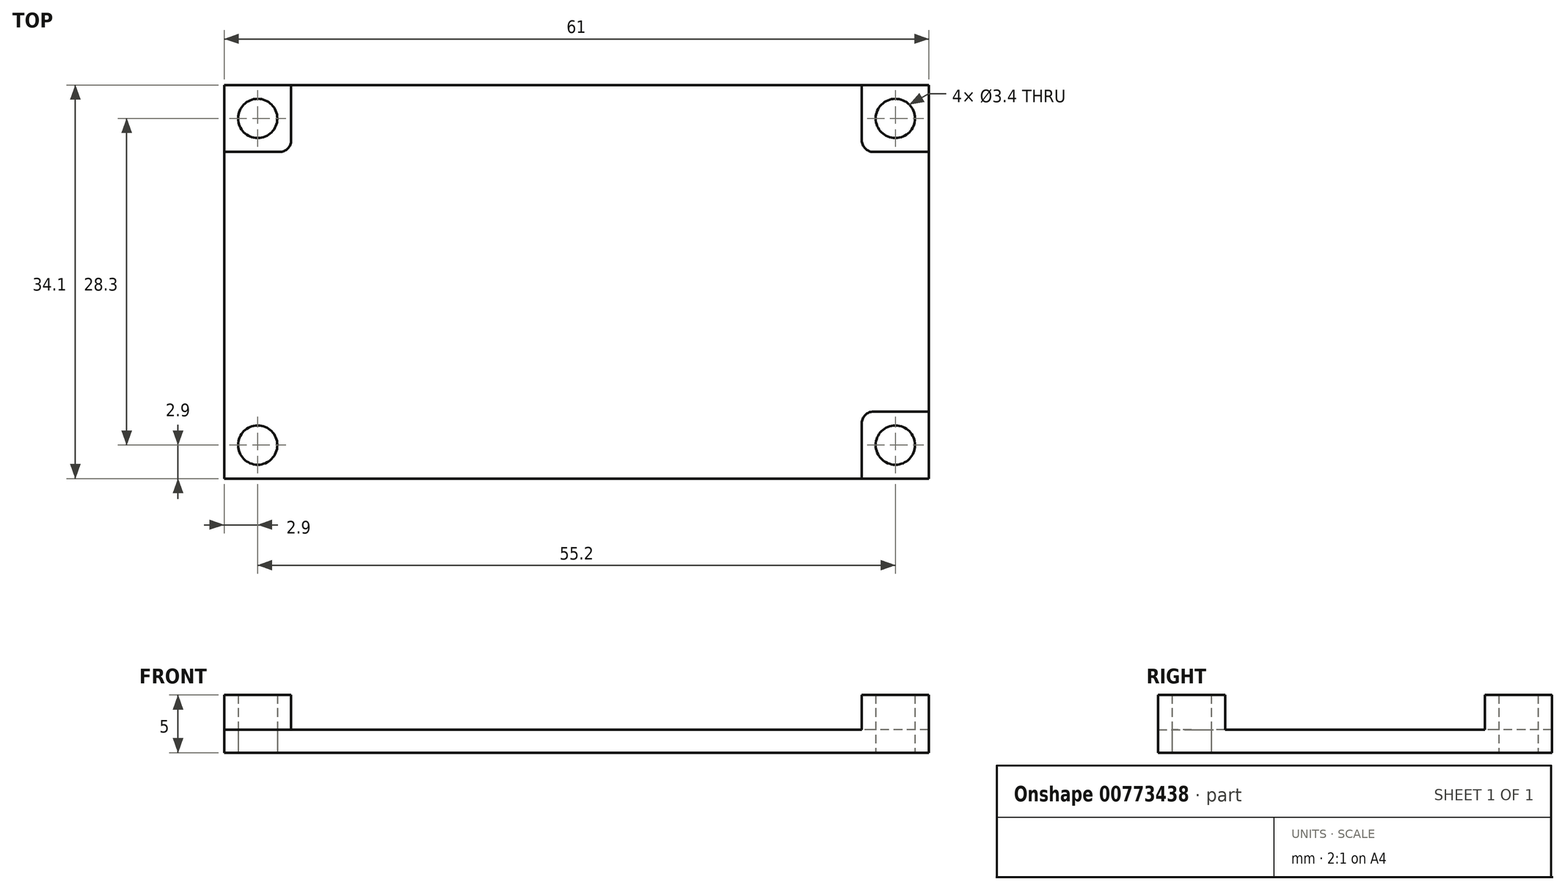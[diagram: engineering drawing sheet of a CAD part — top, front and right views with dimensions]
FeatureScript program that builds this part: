
annotation { "Feature Type Name" : "Feature", "Feature Type Description" : "" }
export const myFeature = defineFeature(function(context is Context, id is Id, definition is map)
    precondition{}
    {
        {
            var Q0;
            Q0=qCreatedBy(makeId("Top.planeOp"),FACE);
            var sketch = newSketch(context, id + "F0", { "sketchPlane" : qUnion([Q0])});
            skLineSegment(sketch, "E0.bottom", {"start": v(30.5, 17.05) * mm, "end": v(-30.5, 17.05) * mm});
            skLineSegment(sketch, "E0.top", {"start": v(30.5, -17.05) * mm, "end": v(-30.5, -17.05) * mm});
            skLineSegment(sketch, "E0.left", {"start": v(30.5, 17.05) * mm, "end": v(30.5, -17.05) * mm});
            skLineSegment(sketch, "E0.right", {"start": v(-30.5, 17.05) * mm, "end": v(-30.5, -17.05) * mm});
            skPoint(sketch, "E0.middle", {"position": v(0, 0) * mm});
            skLineSegment(sketch, "E1.bottom", {"start": v(-27.6, 17.05) * mm, "end": v(27.6, 17.05) * mm, "construction": true});
            skLineSegment(sketch, "E1.top", {"start": v(-27.6, 17.05) * mm, "end": v(27.6, 17.05) * mm, "construction": true});
            skLineSegment(sketch, "E1.left", {"start": v(-27.6, 17.05) * mm, "end": v(-27.6, 17.05) * mm});
            skLineSegment(sketch, "E1.right", {"start": v(27.6, 17.05) * mm, "end": v(27.6, 17.05) * mm});
            skPoint(sketch, "E1.middle", {"position": v(0, 17.05) * mm});
            skLineSegment(sketch, "E2.bottom", {"start": v(-30.5, 14.15) * mm, "end": v(-30.5, 14.15) * mm});
            skLineSegment(sketch, "E2.top", {"start": v(-30.5, -14.15) * mm, "end": v(-30.5, -14.15) * mm});
            skLineSegment(sketch, "E2.left", {"start": v(-30.5, 14.15) * mm, "end": v(-30.5, -14.15) * mm, "construction": true});
            skLineSegment(sketch, "E2.right", {"start": v(-30.5, 14.15) * mm, "end": v(-30.5, -14.15) * mm, "construction": true});
            skPoint(sketch, "E2.middle", {"position": v(-30.5, 0) * mm});
            skPoint(sketch, "E3", {"position": v(-27.6, 14.15) * mm});
            skPoint(sketch, "E4", {"position": v(-27.6, -14.15) * mm});
            skPoint(sketch, "E5", {"position": v(27.6, -14.15) * mm});
            skPoint(sketch, "E6", {"position": v(27.6, 14.15) * mm});
            skSolve(sketch);
        }
        {
            var Q0;
            Q0 = qSketchRegion(id + "F0", true);
            extrude(context, id + "F1", {"entities" : qUnion([Q0]), "depth" : 2 * mm, "offsetDistance" : 25 * mm});
        }
        {
            var Q0;
            Q0=makeQuery(id+"F1.opExtrude","CAP_FACE",FACE,{"disambiguationData":[OSD([sQuery(id+"F0.wireOp",EDGE,"E0.bottom"),sQuery(id+"F0.wireOp",EDGE,"E0.top"),sQuery(id+"F0.wireOp",EDGE,"E0.left"),sQuery(id+"F0.wireOp",EDGE,"E0.right")])],"isStart":false});
            var sketch = newSketch(context, id + "F2", { "sketchPlane" : qUnion([Q0])});
            skLineSegment(sketch, "E7", {"start": v(-27.6, 14.15) * mm, "end": v(-30.5, 14.15) * mm, "construction": true});
            skLineSegment(sketch, "E8", {"start": v(-27.6, 14.15) * mm, "end": v(-24.7, 14.15) * mm, "construction": true});
            skLineSegment(sketch, "E9.bottom", {"start": v(-30.5, 17.05) * mm, "end": v(-24.7, 17.05) * mm});
            skLineSegment(sketch, "E9.top", {"start": v(-30.5, 11.25) * mm, "end": v(-25.7, 11.25) * mm});
            skLineSegment(sketch, "E9.left", {"start": v(-30.5, 17.05) * mm, "end": v(-30.5, 11.25) * mm});
            skLineSegment(sketch, "E9.right", {"start": v(-24.7, 17.05) * mm, "end": v(-24.7, 12.25) * mm});
            skPoint(sketch, "E10.visualSharp", {"position": v(-24.7, 11.25) * mm});
            skArc(sketch, "E10.filletArc", {"start": v(-25.7, 11.25) * mm, "mid": v(-25, 11.54) * mm, "end": v(-24.7, 12.25) * mm});
            skLineSegment(sketch, "E11", {"start": v(-24.7, 11.25) * mm, "end": v(-30.5, 11.25) * mm, "construction": true});
            skLineSegment(sketch, "E12", {"start": v(-24.7, 11.25) * mm, "end": v(-24.7, -17.05) * mm, "construction": true});
            skLineSegment(sketch, "E13", {"start": v(-24.7, 11.25) * mm, "end": v(30.5, 11.25) * mm, "construction": true});
            skLineSegment(sketch, "E14", {"start": v(-24.7, -17.05) * mm, "end": v(-24.7, -12.25) * mm});
            skLineSegment(sketch, "E15", {"start": v(-24.7, -11.25) * mm, "end": v(30.5, -11.25) * mm, "construction": true});
            skLineSegment(sketch, "E16", {"start": v(30.5, -11.25) * mm, "end": v(24.7, -11.25) * mm, "construction": true});
            skLineSegment(sketch, "E17", {"start": v(24.7, -17.05) * mm, "end": v(24.7, 17.05) * mm, "construction": true});
            skLineSegment(sketch, "E18", {"start": v(24.7, 17.05) * mm, "end": v(24.7, 12.25) * mm});
            skLineSegment(sketch, "E19", {"start": v(25.7, 11.25) * mm, "end": v(30.5, 11.25) * mm});
            skLineSegment(sketch, "E20", {"start": v(30.5, -11.25) * mm, "end": v(25.7, -11.25) * mm});
            skLineSegment(sketch, "E21", {"start": v(24.7, -17.05) * mm, "end": v(24.7, -12.25) * mm});
            skPoint(sketch, "E22.visualSharp", {"position": v(-24.7, -11.25) * mm});
            skPoint(sketch, "E23.visualSharp", {"position": v(24.7, -11.25) * mm});
            skArc(sketch, "E23.filletArc", {"start": v(25.7, -11.25) * mm, "mid": v(25, -11.54) * mm, "end": v(24.7, -12.25) * mm});
            skPoint(sketch, "E24.visualSharp", {"position": v(24.7, 11.25) * mm});
            skArc(sketch, "E24.filletArc", {"start": v(24.7, 12.25) * mm, "mid": v(25, 11.54) * mm, "end": v(25.7, 11.25) * mm});
            skLineSegment(sketch, "E25", {"start": v(-24.7, -12.25) * mm, "end": v(-24.7, -17.05) * mm});
            skLineSegment(sketch, "E26", {"start": v(-25.7, -11.25) * mm, "end": v(-30.5, -11.25) * mm});
            skLineSegment(sketch, "E27", {"start": v(-24.7, -12.25) * mm, "end": v(-24.7, -12.25) * mm});
            skArc(sketch, "E28.filletArc", {"start": v(-24.7, -12.25) * mm, "mid": v(-25, -11.54) * mm, "end": v(-25.7, -11.25) * mm});
            skSolve(sketch);
        }
        {
            var Q0;
            Q0 = qSketchRegion(id + "F2", true);
            var Q1;
            {var subQ3=sQuery(id+"F2.wireOp",EDGE,"E25");Q1=makeQuery(id+"F2.imprint","IMPRINT",FACE,{"disambiguationData":[TD([[makeQuery(id+"F2.imprint","IMPRINT",EDGE,{"derivedFrom":subQ3}),-1.0]])]});}
            var Q2;
            {var subQ6=sQuery(id+"F2.wireOp",EDGE,"E20");Q2=makeQuery(id+"F2.imprint","IMPRINT",FACE,{"disambiguationData":[TD([[makeQuery(id+"F2.imprint","IMPRINT",EDGE,{"derivedFrom":subQ6}),1.0]])]});}
            var Q3;
            {var subQ3=sQuery(id+"F2.wireOp",EDGE,"E18");Q3=makeQuery(id+"F2.imprint","IMPRINT",FACE,{"disambiguationData":[TD([[makeQuery(id+"F2.imprint","IMPRINT",EDGE,{"derivedFrom":subQ3}),1.0]])]});}
            extrude(context, id + "F3", {"entities" : qUnion([Q0, Q1, Q2, Q3]), "operationType" : NewBodyOperationType.ADD, "depth" : 3 * mm, "offsetDistance" : 25 * mm});
        }
        {
            var Q0;
            Q0=sQuery(id+"F0.wireOp",VERTEX,"E3");
            var Q1;
            Q1=sQuery(id+"F0.wireOp",VERTEX,"E6");
            var Q2;
            Q2=sQuery(id+"F0.wireOp",VERTEX,"E5");
            var Q3;
            Q3=sQuery(id+"F0.wireOp",VERTEX,"E4");
            var Q4;
            Q4=makeQuery(id+"F1.opExtrude","SWEPT_BODY",BODY,{"disambiguationData":[OSD([sQuery(id+"F0.wireOp",EDGE,"E0.bottom"),sQuery(id+"F0.wireOp",EDGE,"E0.top"),sQuery(id+"F0.wireOp",EDGE,"E0.left"),sQuery(id+"F0.wireOp",EDGE,"E0.right")])]});
            hole(context, id + "F4", {"style" : HoleStyle.SIMPLE, "endStyle" : HoleEndStyle.THROUGH, "oppositeDirection" : true, "standardTappedOrClearance" : lookupTablePath({ "fit" : "Normal", "standard" : "ISO", "size" : "M3", "type" : "Clearance" }), "standardBlindInLast" : lookupTablePath({ "fit" : "Normal", "standard" : "ISO", "size" : "M3", "type" : "Clearance" }), "holeDiameter" : 3.4 * mm, "majorDiameter" : 5 * mm, "tappedDepth" : 12 * mm, "tapClearance" : 3, "startFromSketch" : true, "locations" : qUnion([Q0, Q1, Q2, Q3]), "scope" : qUnion([Q4])});
        }
    });
